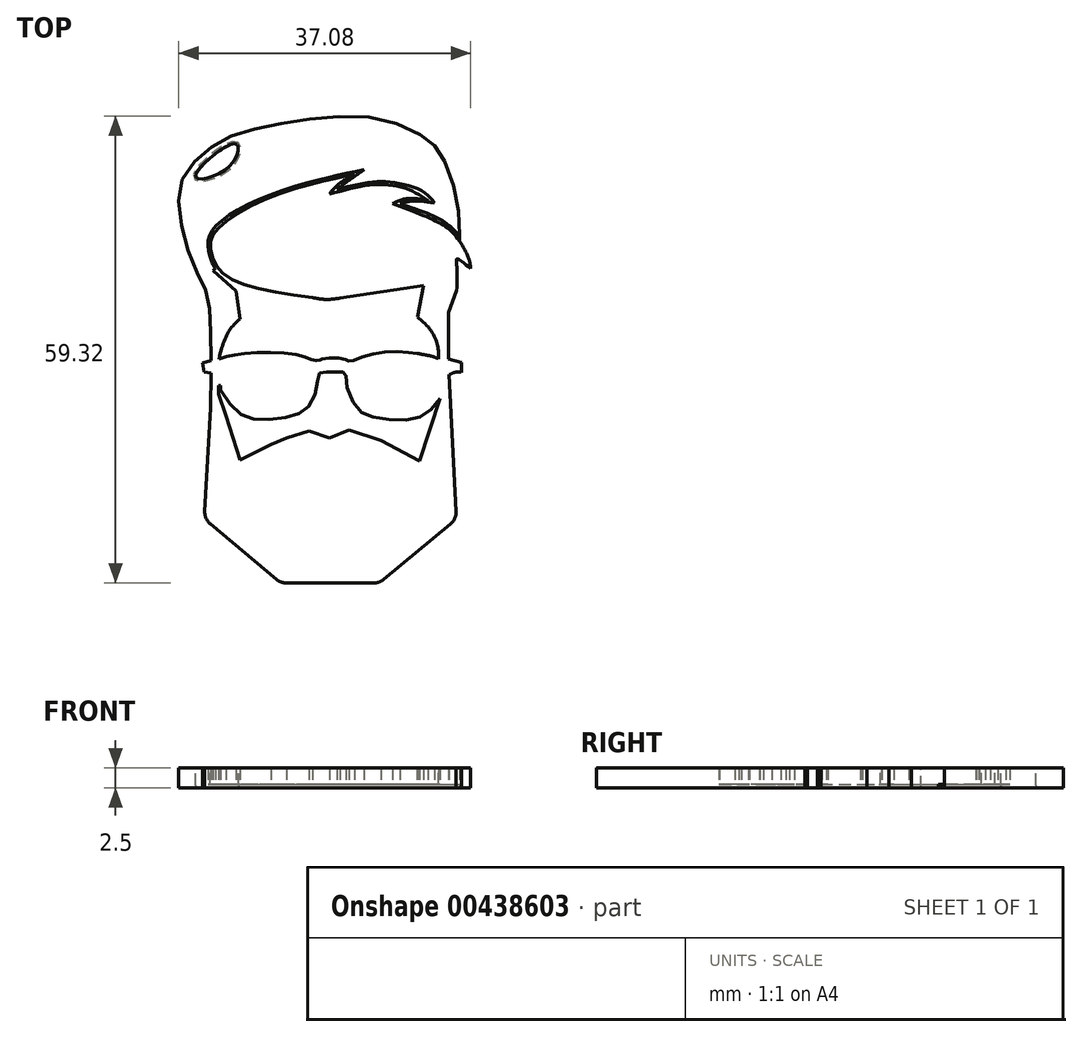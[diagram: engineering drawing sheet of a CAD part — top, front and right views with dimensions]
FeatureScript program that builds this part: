
annotation { "Feature Type Name" : "Feature", "Feature Type Description" : "" }
export const myFeature = defineFeature(function(context is Context, id is Id, definition is map)
    precondition{}
    {
        {
            var Q0;
            Q0=qCreatedBy(makeId("Top.planeOp"),FACE);
            var sketch = newSketch(context, id + "F0", { "sketchPlane" : qUnion([Q0])});
            skLineSegment(sketch, "E0", {"start": v(18.4, -2) * mm, "end": v(19.31, -20.36) * mm});
            skLineSegment(sketch, "E1", {"start": v(19.31, -20.36) * mm, "end": v(9.52, -28.49) * mm});
            skLineSegment(sketch, "E2", {"start": v(9.52, -28.49) * mm, "end": v(-2.99, -28.49) * mm});
            skLineSegment(sketch, "E3", {"start": v(-2.99, -28.49) * mm, "end": v(-12.71, -20.36) * mm});
            skLineSegment(sketch, "E4", {"start": v(-12.71, -20.36) * mm, "end": v(-11.93, -6.22) * mm});
            skLineSegment(sketch, "E5", {"start": v(17.24, -5.05) * mm, "end": v(14.61, -12.96) * mm});
            skLineSegment(sketch, "E6", {"start": v(14.61, -12.96) * mm, "end": v(9.72, -10.4) * mm});
            skLineSegment(sketch, "E7", {"start": v(9.72, -10.4) * mm, "end": v(5.66, -9.05) * mm});
            skLineSegment(sketch, "E8", {"start": v(5.66, -9.05) * mm, "end": v(3.2, -10.08) * mm});
            skLineSegment(sketch, "E9", {"start": v(3.2, -10.08) * mm, "end": v(0.58, -9.16) * mm});
            skLineSegment(sketch, "E10", {"start": v(0.58, -9.16) * mm, "end": v(-2.28, -10.08) * mm});
            skLineSegment(sketch, "E11", {"start": v(-2.28, -10.08) * mm, "end": v(-4.23, -10.9) * mm});
            skLineSegment(sketch, "E12", {"start": v(-4.23, -10.9) * mm, "end": v(-8.17, -12.85) * mm});
            skLineSegment(sketch, "E13", {"start": v(-8.17, -12.85) * mm, "end": v(-9.94, -7.28) * mm});
            skLineSegment(sketch, "E14", {"start": v(-9.94, -7.28) * mm, "end": v(-10.89, -4.45) * mm});
            skLineSegment(sketch, "E15", {"start": v(-10.89, -4.45) * mm, "end": v(-10.89, -3.36) * mm});
            skLineSegment(sketch, "E16", {"start": v(-10.89, -3.36) * mm, "end": v(-10.67, -3.36) * mm});
            skLineSegment(sketch, "E17", {"start": v(-10.67, -3.36) * mm, "end": v(-10.67, -3.97) * mm});
            skFitSpline(sketch, "E18", {"points": [v(-10.67, -3.97) * mm, v(-8.26, -6.95) * mm, v(-5.6, -7.72) * mm, v(-1.75, -7.3) * mm, v(0.3, -6.28) * mm, v(1.53, -3.97) * mm, v(1.81, -2.01) * mm, v(2.07, -1.76) * mm, v(3.03, -1.7) * mm, v(4.16, -1.7) * mm, v(4.93, -1.7) * mm, v(5.28, -1.88) * mm, v(5.31, -3.1) * mm, v(6.7, -6.22) * mm, v(8.4, -7.3) * mm, v(12.44, -7.79) * mm, v(15.3, -7.08) * mm, v(17.24, -5.05) * mm], "startDerivative": vector(27.9, -43) * mm, "endDerivative": vector(25.68, 33.4) * mm});
            skFitSpline(sketch, "E19", {"points": [v(17.03, 0) * mm, v(14.3, 0.7) * mm], "startDerivative": vector(-1.73, 1.07) * mm, "endDerivative": vector(-2.9, 0.55) * mm});
            skFitSpline(sketch, "E20", {"points": [v(14.3, 0.7) * mm, v(8.97, 0.7) * mm, v(5.62, -0.32) * mm, v(5.08, 0) * mm, v(2.27, 0) * mm, v(2.02, -0.16) * mm, v(1.33, -0.2) * mm, v(-0.55, 0.43) * mm, v(-7.5, 0.7) * mm, v(-10.84, 0) * mm], "startDerivative": vector(-20.53, 3) * mm, "endDerivative": vector(-21.02, -7.05) * mm});
            skFitSpline(sketch, "E21", {"points": [v(-10.84, 0) * mm, v(-8.14, 5.05) * mm], "startDerivative": vector(1.64, 8.34) * mm, "endDerivative": vector(3.09, 1.9) * mm});
            skFitSpline(sketch, "E22", {"points": [v(17.03, 0) * mm, v(14.55, 5.11) * mm], "startDerivative": vector(0.27, 4.43) * mm, "endDerivative": vector(-6.63, 4.73) * mm});
            skLineSegment(sketch, "E23", {"start": v(14.55, 5.11) * mm, "end": v(14.39, 5.28) * mm});
            skLineSegment(sketch, "E24", {"start": v(14.39, 5.28) * mm, "end": v(15.13, 9.28) * mm});
            skLineSegment(sketch, "E25", {"start": v(15.13, 9.28) * mm, "end": v(4.53, 7.72) * mm});
            skFitSpline(sketch, "E26", {"points": [v(4.53, 7.72) * mm, v(1.04, 7.77) * mm], "startDerivative": vector(-4.33, -0.72) * mm, "endDerivative": vector(-4.73, 0.85) * mm});
            skFitSpline(sketch, "E27", {"points": [v(1.04, 7.77) * mm, v(-8.8, 9.88) * mm, v(-11.48, 12.33) * mm, v(-11.92, 14.8) * mm, v(-10.9, 16.64) * mm, v(-5.47, 20.05) * mm, v(2.46, 22.57) * mm, v(6.35, 23.49) * mm], "startDerivative": vector(-55.4, 7.74) * mm, "endDerivative": vector(27.26, 6.17) * mm});
            skFitSpline(sketch, "E28", {"points": [v(6.35, 23.49) * mm, v(3.2, 20.92) * mm], "startDerivative": vector(-2.88, -1.95) * mm, "endDerivative": vector(-1.95, -3.75) * mm});
            skFitSpline(sketch, "E29", {"points": [v(3.2, 20.92) * mm, v(8.85, 22.12) * mm, v(13.08, 21.56) * mm, v(15.68, 20.12) * mm], "startDerivative": vector(14.83, 4.19) * mm, "endDerivative": vector(8.62, -5.77) * mm});
            skFitSpline(sketch, "E30", {"points": [v(15.68, 20.12) * mm, v(11.22, 19.7) * mm], "startDerivative": vector(-5.99, 1.23) * mm, "endDerivative": vector(-4.18, -2.45) * mm});
            skFitSpline(sketch, "E31", {"points": [v(11.22, 19.7) * mm, v(16.7, 17.5) * mm, v(19.17, 15.67) * mm, v(20.91, 12.63) * mm, v(21.1, 11.48) * mm], "startDerivative": vector(17.94, -6.42) * mm, "endDerivative": vector(0.4, -6.63) * mm});
            skFitSpline(sketch, "E32", {"points": [v(21.1, 11.48) * mm, v(19.37, 12.7) * mm, v(19.34, 11.97) * mm, v(19.35, 8.66) * mm], "startDerivative": vector(-6.46, 5.48) * mm, "endDerivative": vector(-0.2, -8.45) * mm});
            skLineSegment(sketch, "E33", {"start": v(19.35, 8.66) * mm, "end": v(18.33, 5.86) * mm});
            skLineSegment(sketch, "E34", {"start": v(18.33, 5.86) * mm, "end": v(18.33, 0) * mm});
            skLineSegment(sketch, "E35", {"start": v(18.33, 0) * mm, "end": v(19.99, -0.45) * mm});
            skLineSegment(sketch, "E36", {"start": v(19.99, -0.45) * mm, "end": v(19.99, -1.71) * mm});
            skFitSpline(sketch, "E37", {"points": [v(19.99, -1.71) * mm, v(18.4, -2) * mm], "startDerivative": vector(-1.95, 0.32) * mm, "endDerivative": vector(-1.73, -0.88) * mm});
            skLineSegment(sketch, "E38", {"start": v(-8.14, 5.05) * mm, "end": v(-8.68, 8.6) * mm});
            skLineSegment(sketch, "E39", {"start": v(-8.68, 8.6) * mm, "end": v(-11.63, 11.2) * mm});
            skLineSegment(sketch, "E40", {"start": v(-11.63, 11.2) * mm, "end": v(-11.3, 11.56) * mm});
            skFitSpline(sketch, "E41", {"points": [v(-11.3, 11.56) * mm, v(-12.16, 13.59) * mm, v(-12.17, 15.25) * mm, v(-11.14, 16.95) * mm, v(-6.2, 20.08) * mm, v(2.56, 22.92) * mm, v(7.58, 24.03) * mm], "startDerivative": vector(-12.08, 14.9) * mm, "endDerivative": vector(24.09, 4.89) * mm});
            skFitSpline(sketch, "E42", {"points": [v(7.58, 24.03) * mm, v(4.14, 21.51) * mm], "startDerivative": vector(-3.43, -2.52) * mm, "endDerivative": vector(-2.96, -2.58) * mm});
            skFitSpline(sketch, "E43", {"points": [v(4.14, 21.51) * mm, v(8.5, 22.45) * mm, v(11.69, 22.34) * mm, v(15.05, 21.26) * mm, v(16.54, 19.8) * mm], "startDerivative": vector(15.6, 4.02) * mm, "endDerivative": vector(6.16, -7.84) * mm});
            skFitSpline(sketch, "E44", {"points": [v(16.54, 19.8) * mm, v(13.9, 20.06) * mm, v(12.14, 19.73) * mm], "startDerivative": vector(-5.07, 0.8) * mm, "endDerivative": vector(-3.7, -1.01) * mm});
            skFitSpline(sketch, "E45", {"points": [v(12.14, 19.73) * mm, v(16.04, 18.31) * mm, v(17.69, 17.44) * mm, v(19.7, 15.73) * mm], "startDerivative": vector(10.7, -3.73) * mm, "endDerivative": vector(6.18, -5.99) * mm});
            skFitSpline(sketch, "E46", {"points": [v(19.7, 15.73) * mm, v(19.17, 20.96) * mm, v(17.3, 26.1) * mm, v(15.65, 27.83) * mm, v(10.86, 30.2) * mm, v(3.36, 30.74) * mm, v(-3.98, 29.67) * mm, v(-9.4, 28.27) * mm, v(-13.1, 25.9) * mm, v(-15.6, 22.54) * mm, v(-15.8, 18.06) * mm, v(-14.35, 12.51) * mm, v(-12.64, 8.98) * mm, v(-12, 5.95) * mm, v(-11.84, -0.2) * mm], "startDerivative": vector(1.23, 69.28) * mm, "endDerivative": vector(0.67, -84.51) * mm});
            skLineSegment(sketch, "E47", {"start": v(-11.84, -0.2) * mm, "end": v(-12.94, -0.52) * mm});
            skLineSegment(sketch, "E48", {"start": v(-12.94, -0.52) * mm, "end": v(-12.76, -1.66) * mm});
            skLineSegment(sketch, "E49", {"start": v(-12.76, -1.66) * mm, "end": v(-11.84, -1.8) * mm});
            skLineSegment(sketch, "E50", {"start": v(-11.84, -1.8) * mm, "end": v(-11.93, -6.22) * mm});
            skLineSegment(sketch, "E51", {"start": v(19.7, 15.73) * mm, "end": v(19.7, 14.96) * mm});
            skSolve(sketch);
        }
        {
            var Q0;
            Q0=makeQuery(id+"F0.imprint","IMPRINT",FACE,{"disambiguationData":[TD([[makeQuery(id+"F0.imprint","IMPRINT",EDGE,{"derivedFrom":sQuery(id+"F0.wireOp",EDGE,"E0")}),-1.0]])]});
            extrude(context, id + "F1", {"entities" : qUnion([Q0]), "depth" : 2.5 * mm});
        }
        {
            var Q0;
            Q0=makeQuery(id+"F0.imprint","IMPRINT",FACE,{"disambiguationData":[TD([[makeQuery(id+"F0.imprint","IMPRINT",EDGE,{"derivedFrom":sQuery(id+"F0.wireOp",EDGE,"E19")}),-1.0]])]});
            var Q1;
            Q1=makeQuery(id+"F0.imprint","IMPRINT",FACE,{"disambiguationData":[TD([[makeQuery(id+"F0.imprint","IMPRINT",EDGE,{"derivedFrom":sQuery(id+"F0.wireOp",EDGE,"E5")}),-1.0]])]});
            extrude(context, id + "F2", {"entities" : qUnion([Q0, Q1]), "operationType" : NewBodyOperationType.ADD, "depth" : .4 * mm});
        }
        {
            var Q0;
            Q0=makeQuery(id+"F1.opExtrude","CAP_FACE",FACE,{"disambiguationData":[OSD([sQuery(id+"F0.wireOp",EDGE,"E0"),sQuery(id+"F0.wireOp",EDGE,"E1"),sQuery(id+"F0.wireOp",EDGE,"E2"),sQuery(id+"F0.wireOp",EDGE,"E3"),sQuery(id+"F0.wireOp",EDGE,"E4"),sQuery(id+"F0.wireOp",EDGE,"E5"),sQuery(id+"F0.wireOp",EDGE,"E6"),sQuery(id+"F0.wireOp",EDGE,"E7"),sQuery(id+"F0.wireOp",EDGE,"E8"),sQuery(id+"F0.wireOp",EDGE,"E9"),sQuery(id+"F0.wireOp",EDGE,"E10"),sQuery(id+"F0.wireOp",EDGE,"E11"),sQuery(id+"F0.wireOp",EDGE,"E12"),sQuery(id+"F0.wireOp",EDGE,"E13"),sQuery(id+"F0.wireOp",EDGE,"E14"),sQuery(id+"F0.wireOp",EDGE,"E15"),sQuery(id+"F0.wireOp",EDGE,"E16"),sQuery(id+"F0.wireOp",EDGE,"E17"),sQuery(id+"F0.wireOp",EDGE,"E18"),sQuery(id+"F0.wireOp",EDGE,"E19"),sQuery(id+"F0.wireOp",EDGE,"E20"),sQuery(id+"F0.wireOp",EDGE,"E21"),sQuery(id+"F0.wireOp",EDGE,"E22"),sQuery(id+"F0.wireOp",EDGE,"E23"),sQuery(id+"F0.wireOp",EDGE,"E24"),sQuery(id+"F0.wireOp",EDGE,"E25"),sQuery(id+"F0.wireOp",EDGE,"E26"),sQuery(id+"F0.wireOp",EDGE,"E27"),sQuery(id+"F0.wireOp",EDGE,"E28"),sQuery(id+"F0.wireOp",EDGE,"E29"),sQuery(id+"F0.wireOp",EDGE,"E30"),sQuery(id+"F0.wireOp",EDGE,"E31"),sQuery(id+"F0.wireOp",EDGE,"E32"),sQuery(id+"F0.wireOp",EDGE,"E33"),sQuery(id+"F0.wireOp",EDGE,"E34"),sQuery(id+"F0.wireOp",EDGE,"E35"),sQuery(id+"F0.wireOp",EDGE,"E36"),sQuery(id+"F0.wireOp",EDGE,"E37"),sQuery(id+"F0.wireOp",EDGE,"E38"),sQuery(id+"F0.wireOp",EDGE,"E39"),sQuery(id+"F0.wireOp",EDGE,"E40"),sQuery(id+"F0.wireOp",EDGE,"E41"),sQuery(id+"F0.wireOp",EDGE,"E42"),sQuery(id+"F0.wireOp",EDGE,"E43"),sQuery(id+"F0.wireOp",EDGE,"E44"),sQuery(id+"F0.wireOp",EDGE,"E45"),sQuery(id+"F0.wireOp",EDGE,"E46"),sQuery(id+"F0.wireOp",EDGE,"E47"),sQuery(id+"F0.wireOp",EDGE,"E48"),sQuery(id+"F0.wireOp",EDGE,"E49"),sQuery(id+"F0.wireOp",EDGE,"E50")])],"isStart":false});
            var sketch = newSketch(context, id + "F3", { "sketchPlane" : qUnion([Q0])});
            skFitSpline(sketch, "E52", {"points": [v(-8.58, 27.24) * mm, v(-12.13, 25.37) * mm, v(-13.73, 23) * mm, v(-9.61, 24.37) * mm, v(-8.58, 27.24) * mm]});
            skSolve(sketch);
        }
        {
            var Q0;
            Q0=makeQuery(id+"F3.imprint","IMPRINT",FACE,{"disambiguationData":[TD([[makeQuery(id+"F3.imprint","IMPRINT",EDGE,{"derivedFrom":sQuery(id+"F3.wireOp",EDGE,"E52")}),1.0]])]});
            extrude(context, id + "F4", {"entities" : qUnion([Q0]), "operationType" : NewBodyOperationType.REMOVE, "oppositeDirection" : true, "depth" : 25 * mm});
        }
        {
            var Q0;
            Q0=makeQuery(id+"F4.boolean.opBoolean","COPY",EDGE,{"derivedFrom":makeQuery(id+"F4.opExtrude","CAP_EDGE",EDGE,{"disambiguationData":[OSD([sQuery(id+"F3.wireOp",EDGE,"E52")])],"isStart":true})});
            var Q1;
            {var subQ0=sQuery(id+"F0.wireOp",EDGE,"E45");var subQ1=sQuery(id+"F0.wireOp",EDGE,"E44");var subQ2=sQuery(id+"F0.wireOp",EDGE,"E43");var subQ3=sQuery(id+"F0.wireOp",EDGE,"E42");var subQ4=sQuery(id+"F0.wireOp",EDGE,"E41");var subQ5=sQuery(id+"F0.wireOp",EDGE,"E40");var subQ6=sQuery(id+"F0.wireOp",EDGE,"E39");var subQ7=sQuery(id+"F0.wireOp",EDGE,"E38");var subQ8=sQuery(id+"F0.wireOp",EDGE,"E31");var subQ9=sQuery(id+"F0.wireOp",EDGE,"E30");var subQ10=sQuery(id+"F0.wireOp",EDGE,"E29");var subQ11=sQuery(id+"F0.wireOp",EDGE,"E28");var subQ12=sQuery(id+"F0.wireOp",EDGE,"E27");var subQ13=sQuery(id+"F0.wireOp",EDGE,"E26");var subQ14=sQuery(id+"F0.wireOp",EDGE,"E25");var subQ15=sQuery(id+"F0.wireOp",EDGE,"E24");var subQ16=sQuery(id+"F0.wireOp",EDGE,"E23");var subQ17=sQuery(id+"F0.wireOp",EDGE,"E22");var subQ18=sQuery(id+"F0.wireOp",EDGE,"E21");var subQ19=sQuery(id+"F0.wireOp",EDGE,"E20");var subQ20=sQuery(id+"F0.wireOp",EDGE,"E19");var subQ21=sQuery(id+"F0.wireOp",EDGE,"E18");var subQ22=sQuery(id+"F0.wireOp",EDGE,"E17");var subQ23=sQuery(id+"F0.wireOp",EDGE,"E16");var subQ24=sQuery(id+"F0.wireOp",EDGE,"E15");var subQ25=sQuery(id+"F0.wireOp",EDGE,"E14");var subQ26=sQuery(id+"F0.wireOp",EDGE,"E13");var subQ27=sQuery(id+"F0.wireOp",EDGE,"E12");var subQ28=sQuery(id+"F0.wireOp",EDGE,"E11");var subQ29=sQuery(id+"F0.wireOp",EDGE,"E10");var subQ30=sQuery(id+"F0.wireOp",EDGE,"E9");var subQ31=sQuery(id+"F0.wireOp",EDGE,"E8");var subQ32=sQuery(id+"F0.wireOp",EDGE,"E7");var subQ33=sQuery(id+"F0.wireOp",EDGE,"E6");var subQ34=sQuery(id+"F0.wireOp",EDGE,"E5");Q1=makeQuery(id+"F4.boolean.opBoolean","INTERSECT",EDGE,{"derivedFrom":[makeQuery(id+"F2.boolean.opBoolean","MERGE",FACE,{"derivedFrom":[makeQuery(id+"F1.opExtrude","CAP_FACE",FACE,{"disambiguationData":[OSD([sQuery(id+"F0.wireOp",EDGE,"E0"),sQuery(id+"F0.wireOp",EDGE,"E1"),sQuery(id+"F0.wireOp",EDGE,"E2"),sQuery(id+"F0.wireOp",EDGE,"E3"),sQuery(id+"F0.wireOp",EDGE,"E4"),subQ34,subQ33,subQ32,subQ31,subQ30,subQ29,subQ28,subQ27,subQ26,subQ25,subQ24,subQ23,subQ22,subQ21,subQ20,subQ19,subQ18,subQ17,subQ16,subQ15,subQ14,subQ13,subQ12,subQ11,subQ10,subQ9,subQ8,sQuery(id+"F0.wireOp",EDGE,"E32"),sQuery(id+"F0.wireOp",EDGE,"E33"),sQuery(id+"F0.wireOp",EDGE,"E34"),sQuery(id+"F0.wireOp",EDGE,"E35"),sQuery(id+"F0.wireOp",EDGE,"E36"),sQuery(id+"F0.wireOp",EDGE,"E37"),subQ7,subQ6,subQ5,subQ4,subQ3,subQ2,subQ1,subQ0,sQuery(id+"F0.wireOp",EDGE,"E46"),sQuery(id+"F0.wireOp",EDGE,"E47"),sQuery(id+"F0.wireOp",EDGE,"E48"),sQuery(id+"F0.wireOp",EDGE,"E49"),sQuery(id+"F0.wireOp",EDGE,"E50")])],"isStart":true}),makeQuery(id+"F2.opExtrude","CAP_FACE",FACE,{"disambiguationData":[OSD([subQ34,subQ33,subQ32,subQ31,subQ30,subQ29,subQ28,subQ27,subQ26,subQ25,subQ24,subQ23,subQ22,subQ21])],"isStart":true}),makeQuery(id+"F2.opExtrude","CAP_FACE",FACE,{"disambiguationData":[OSD([subQ20,subQ19,subQ18,subQ17,subQ16,subQ15,subQ14,subQ13,subQ12,subQ11,subQ10,subQ9,subQ8,subQ7,subQ6,subQ5,subQ4,subQ3,subQ2,subQ1,subQ0,sQuery(id+"F0.wireOp",EDGE,"E51")])],"isStart":true})]}),makeQuery(id+"F4.opExtrude","SWEPT_FACE",FACE,{"disambiguationData":[OSD([sQuery(id+"F3.wireOp",EDGE,"E52")])]})]});}
            fillet(context, id + "F5", {"entities" : qUnion([Q0, Q1]), "radius" : .3 * mm, "tangentPropagation" : true, "allowEdgeOverflow" : false});
        }
        {
            var Q0;
            Q0=makeQuery(id+"F1.opExtrude","SWEPT_EDGE",EDGE,{"disambiguationData":[OSD([sQuery(id+"F0.wireOp",EDGE,"E3"),sQuery(id+"F0.wireOp",EDGE,"E4")])]});
            var Q1;
            Q1=makeQuery(id+"F1.opExtrude","SWEPT_EDGE",EDGE,{"disambiguationData":[OSD([sQuery(id+"F0.wireOp",EDGE,"E2"),sQuery(id+"F0.wireOp",EDGE,"E3")])]});
            var Q2;
            Q2=makeQuery(id+"F1.opExtrude","SWEPT_EDGE",EDGE,{"disambiguationData":[OSD([sQuery(id+"F0.wireOp",EDGE,"E1"),sQuery(id+"F0.wireOp",EDGE,"E2")])]});
            var Q3;
            Q3=makeQuery(id+"F1.opExtrude","SWEPT_EDGE",EDGE,{"disambiguationData":[OSD([sQuery(id+"F0.wireOp",EDGE,"E0"),sQuery(id+"F0.wireOp",EDGE,"E1")])]});
            fillet(context, id + "F6", {"entities" : qUnion([Q0, Q1, Q2, Q3]), "radius" : 2 * mm, "tangentPropagation" : true, "allowEdgeOverflow" : false});
        }
    });
